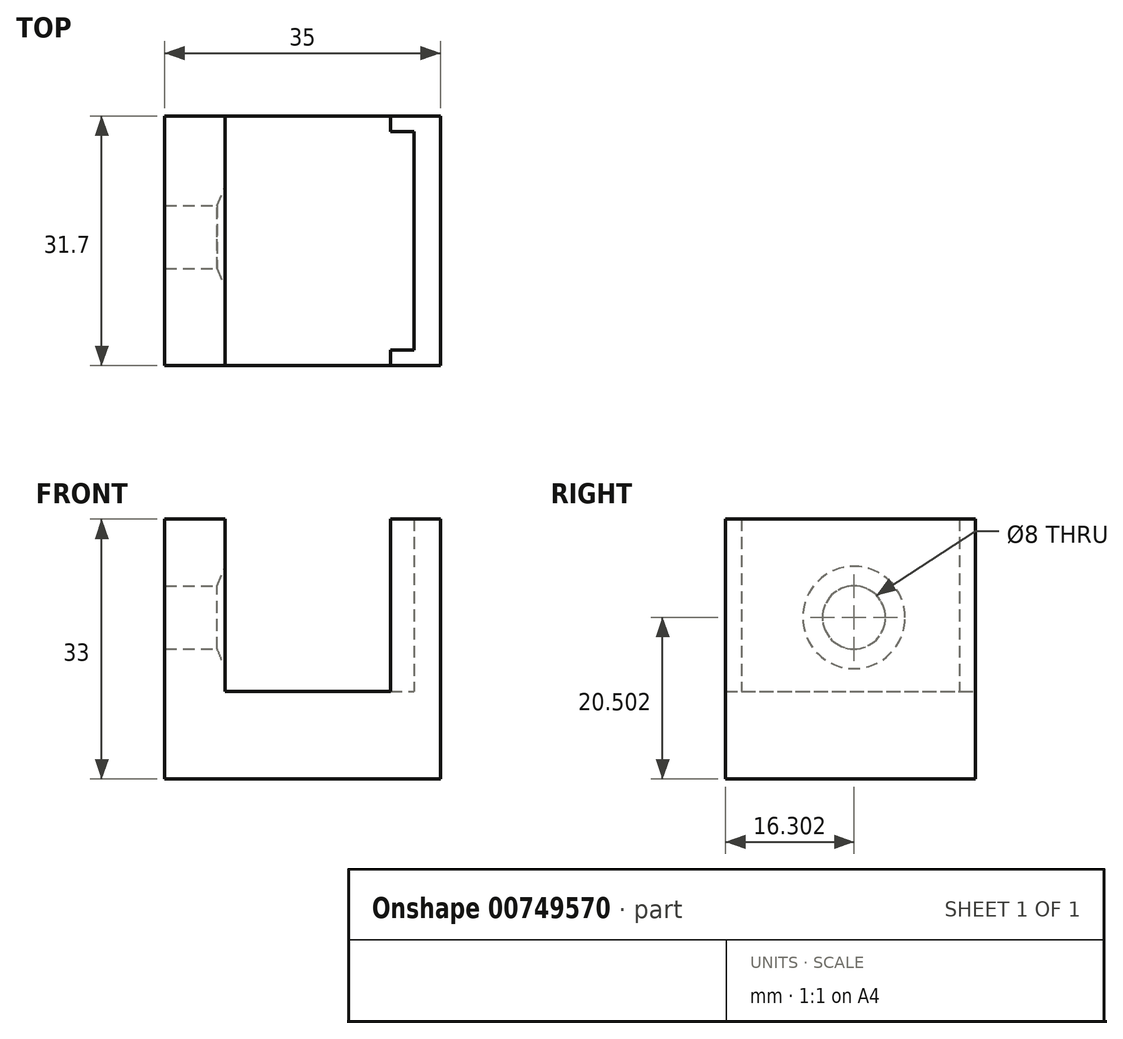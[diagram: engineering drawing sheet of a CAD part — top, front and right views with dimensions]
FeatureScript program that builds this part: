
annotation { "Feature Type Name" : "Feature", "Feature Type Description" : "" }
export const myFeature = defineFeature(function(context is Context, id is Id, definition is map)
    precondition{}
    {
        {
            var Q0;
            Q0=qCreatedBy(makeId("Front.planeOp"),FACE);
            var sketch = newSketch(context, id + "F0", { "sketchPlane" : qUnion([Q0])});
            skLineSegment(sketch, "E0", {"start": v(0, 20.67) * mm, "end": v(10.2, 20.67) * mm});
            skLineSegment(sketch, "E1", {"start": v(39.6, 0) * mm, "end": v(39.6, 20.67) * mm});
            skLineSegment(sketch, "E2", {"start": v(39.6, 20.67) * mm, "end": v(42.8, 20.67) * mm});
            skLineSegment(sketch, "E3", {"start": v(0, -5.53) * mm, "end": v(0, 2.33) * mm});
            skLineSegment(sketch, "E4", {"start": v(0, 20.67) * mm, "end": v(0, -8.15) * mm});
            skLineSegment(sketch, "E5", {"start": v(42.8, 20.67) * mm, "end": v(42.8, -8.15) * mm});
            skLineSegment(sketch, "E6", {"start": v(10.2, 20.67) * mm, "end": v(10.2, -4.65) * mm});
            skLineSegment(sketch, "E7", {"start": v(10.2, -4.65) * mm, "end": v(39.6, -4.65) * mm});
            skLineSegment(sketch, "E8", {"start": v(39.6, -4.65) * mm, "end": v(39.6, 3.49) * mm});
            skLineSegment(sketch, "E9", {"start": v(39.4, -42.26) * mm, "end": v(39.4, -9.26) * mm});
            skLineSegment(sketch, "E10", {"start": v(39.4, -9.26) * mm, "end": v(36.06, -9.26) * mm});
            skLineSegment(sketch, "E11", {"start": v(36.06, -9.26) * mm, "end": v(36.06, -31.13) * mm});
            skLineSegment(sketch, "E12", {"start": v(36.06, -31.13) * mm, "end": v(12.06, -31.13) * mm});
            skLineSegment(sketch, "E13", {"start": v(12.06, -31.13) * mm, "end": v(12.06, -9.26) * mm});
            skLineSegment(sketch, "E14", {"start": v(39.4, -42.26) * mm, "end": v(4.4, -42.26) * mm});
            skLineSegment(sketch, "E15", {"start": v(4.4, -42.26) * mm, "end": v(4.4, -9.26) * mm});
            skLineSegment(sketch, "E16", {"start": v(4.4, -9.26) * mm, "end": v(12.06, -9.26) * mm});
            skSolve(sketch);
        }
        {
            var Q0;
            Q0=makeQuery(id+"F0.imprint","IMPRINT",FACE,{"disambiguationData":[TD([[makeQuery(id+"F0.imprint","IMPRINT",EDGE,{"derivedFrom":sQuery(id+"F0.wireOp",EDGE,"E9")}),1.0]])]});
            extrude(context, id + "F1", {"entities" : qUnion([Q0]), "depth" : 31.7 * mm, "offsetDistance" : 25 * mm});
        }
        {
            var Q0;
            Q0=makeQuery(id+"F1.opExtrude","SWEPT_FACE",FACE,{"disambiguationData":[OSD([sQuery(id+"F0.wireOp",EDGE,"E11")])]});
            var sketch = newSketch(context, id + "F2", { "sketchPlane" : qUnion([Q0])});
            skLineSegment(sketch, "E17.bottom", {"start": v(0, -9.26) * mm, "end": v(2, -9.26) * mm});
            skLineSegment(sketch, "E17.top", {"start": v(0, -37.8) * mm, "end": v(2, -37.8) * mm});
            skLineSegment(sketch, "E17.left", {"start": v(0, -9.26) * mm, "end": v(0, -37.8) * mm});
            skLineSegment(sketch, "E17.right", {"start": v(2, -9.26) * mm, "end": v(2, -37.8) * mm});
            skLineSegment(sketch, "E18.bottom", {"start": v(31.7, -9.26) * mm, "end": v(29.7, -9.26) * mm});
            skLineSegment(sketch, "E18.top", {"start": v(31.7, -37.8) * mm, "end": v(29.7, -37.8) * mm});
            skLineSegment(sketch, "E18.left", {"start": v(31.7, -9.26) * mm, "end": v(31.7, -37.8) * mm});
            skLineSegment(sketch, "E18.right", {"start": v(29.7, -9.26) * mm, "end": v(29.7, -37.8) * mm});
            skSolve(sketch);
        }
        {
            var Q0;
            {var subQ0=sQuery(id+"F2.wireOp",EDGE,"E17.bottom");Q0=makeQuery(id+"F2.imprint","IMPRINT",FACE,{"disambiguationData":[TD([[makeQuery(id+"F2.imprint","IMPRINT",EDGE,{"derivedFrom":subQ0}),1.0]])]});}
            var Q1;
            {var subQ0=sQuery(id+"F2.wireOp",EDGE,"E18.bottom");Q1=makeQuery(id+"F2.imprint","IMPRINT",FACE,{"disambiguationData":[TD([[makeQuery(id+"F2.imprint","IMPRINT",EDGE,{"derivedFrom":subQ0}),1.0]])]});}
            extrude(context, id + "F3", {"entities" : qUnion([Q0, Q1]), "operationType" : NewBodyOperationType.ADD, "depth" : 3 * mm, "offsetDistance" : 25 * mm});
        }
        {
            var Q0;
            Q0=makeQuery(id+"F1.opExtrude","SWEPT_FACE",FACE,{"disambiguationData":[OSD([sQuery(id+"F0.wireOp",EDGE,"E13")])]});
            var sketch = newSketch(context, id + "F4", { "sketchPlane" : qUnion([Q0])});
            skPoint(sketch, "E19", {"position": v(-15.4, -21.76) * mm});
            skSolve(sketch);
        }
        {
            var Q0;
            Q0=sQuery(id+"F4.wireOp",VERTEX,"E19");
            var Q1;
            Q1=makeQuery(id+"F1.opExtrude","SWEPT_BODY",BODY,{"disambiguationData":[OSD([sQuery(id+"F0.wireOp",EDGE,"E9"),sQuery(id+"F0.wireOp",EDGE,"E10"),sQuery(id+"F0.wireOp",EDGE,"E11"),sQuery(id+"F0.wireOp",EDGE,"E12"),sQuery(id+"F0.wireOp",EDGE,"E13"),sQuery(id+"F0.wireOp",EDGE,"E14"),sQuery(id+"F0.wireOp",EDGE,"E15"),sQuery(id+"F0.wireOp",EDGE,"E16")])]});
            hole(context, id + "F5", {"style" : HoleStyle.C_SINK, "endStyle" : HoleEndStyle.THROUGH, "holeDiameter" : 8 * mm, "cSinkDiameter" : 13 * mm, "cSinkAngle" : 135 * degree, "majorDiameter" : 5 * mm, "isTappedThrough" : true, "tappedDepth" : 12 * mm, "tapClearance" : 3, "startFromSketch" : true, "locations" : qUnion([Q0]), "scope" : qUnion([Q1])});
        }
    });
